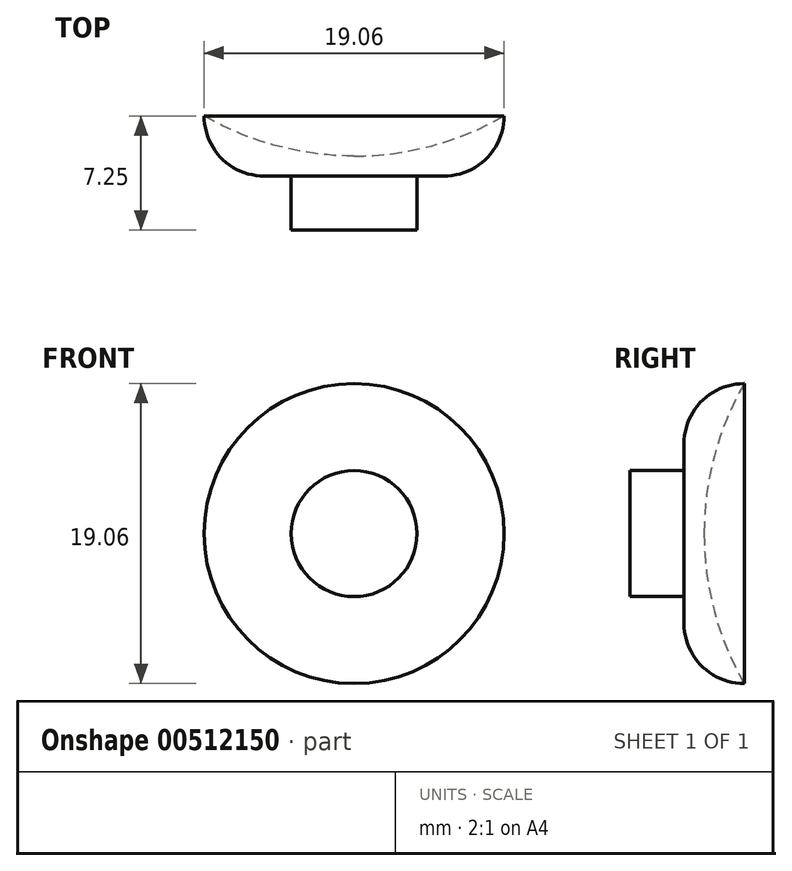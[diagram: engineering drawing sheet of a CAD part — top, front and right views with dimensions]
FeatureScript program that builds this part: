
annotation { "Feature Type Name" : "Feature", "Feature Type Description" : "" }
export const myFeature = defineFeature(function(context is Context, id is Id, definition is map)
    precondition{}
    {
        {
            var Q0;
            Q0=qCreatedBy(makeId("Top.planeOp"),FACE);
            var sketch = newSketch(context, id + "F0", { "sketchPlane" : qUnion([Q0])});
            skLineSegment(sketch, "E0", {"start": v(0, -6.35) * mm, "end": v(0, 31.75) * mm});
            skArc(sketch, "E1", {"start": v(0, -6.35) * mm, "mid": v(19.05, 12.7) * mm, "end": v(0, 31.75) * mm});
            skSolve(sketch);
        }
        {
            var Q0;
            Q0=qCreatedBy(makeId("Front.planeOp"),FACE);
            var sketch = newSketch(context, id + "F1", { "sketchPlane" : qUnion([Q0])});
            skCircle(sketch, "E2", {"center": v(0, 0) * mm, "radius": 9.53 * mm});
            skSolve(sketch);
        }
        {
            var Q0;
            Q0 = qSketchRegion(id + "F1", true);
            extrude(context, id + "F2", {"entities" : qUnion([Q0]), "depth" : 7.62 * mm});
        }
        {
            var Q0;
            Q0=makeQuery(id+"F0.imprint","IMPRINT",FACE,{"disambiguationData":[TD([[makeQuery(id+"F0.imprint","IMPRINT",EDGE,{"derivedFrom":sQuery(id+"F0.wireOp",EDGE,"E0")}),-1.0]])]});
            var Q1;
            Q1=sQuery(id+"F0.wireOp",EDGE,"E0");
            revolve(context, id + "F3", {"operationType" : NewBodyOperationType.REMOVE, "entities" : qUnion([Q0]), "axis" : qUnion([Q1]), "revolveType" : RevolveType.FULL, "oppositeDirection" : true});
        }
        {
            var Q0;
            Q0=makeQuery(id+"F2.opExtrude","CAP_FACE",FACE,{"disambiguationData":[OSD([sQuery(id+"F1.wireOp",EDGE,"E2")])],"isStart":false});
            var sketch = newSketch(context, id + "F4", { "sketchPlane" : qUnion([Q0])});
            skCircle(sketch, "E3", {"center": v(0, 0) * mm, "radius": 4 * mm});
            skSolve(sketch);
        }
        {
            var Q0;
            Q0 = qSketchRegion(id + "F4", true);
            extrude(context, id + "F5", {"entities" : qUnion([Q0]), "operationType" : NewBodyOperationType.ADD, "depth" : 3.43 * mm});
        }
        {
            var Q0;
            Q0=makeQuery(id+"F2.opExtrude","CAP_EDGE",EDGE,{"disambiguationData":[OSD([sQuery(id+"F1.wireOp",EDGE,"E2")])],"isStart":false});
            fillet(context, id + "F6", {"entities" : qUnion([Q0]), "radius" : 3.8 * mm, "tangentPropagation" : true, "allowEdgeOverflow" : false});
        }
    });
